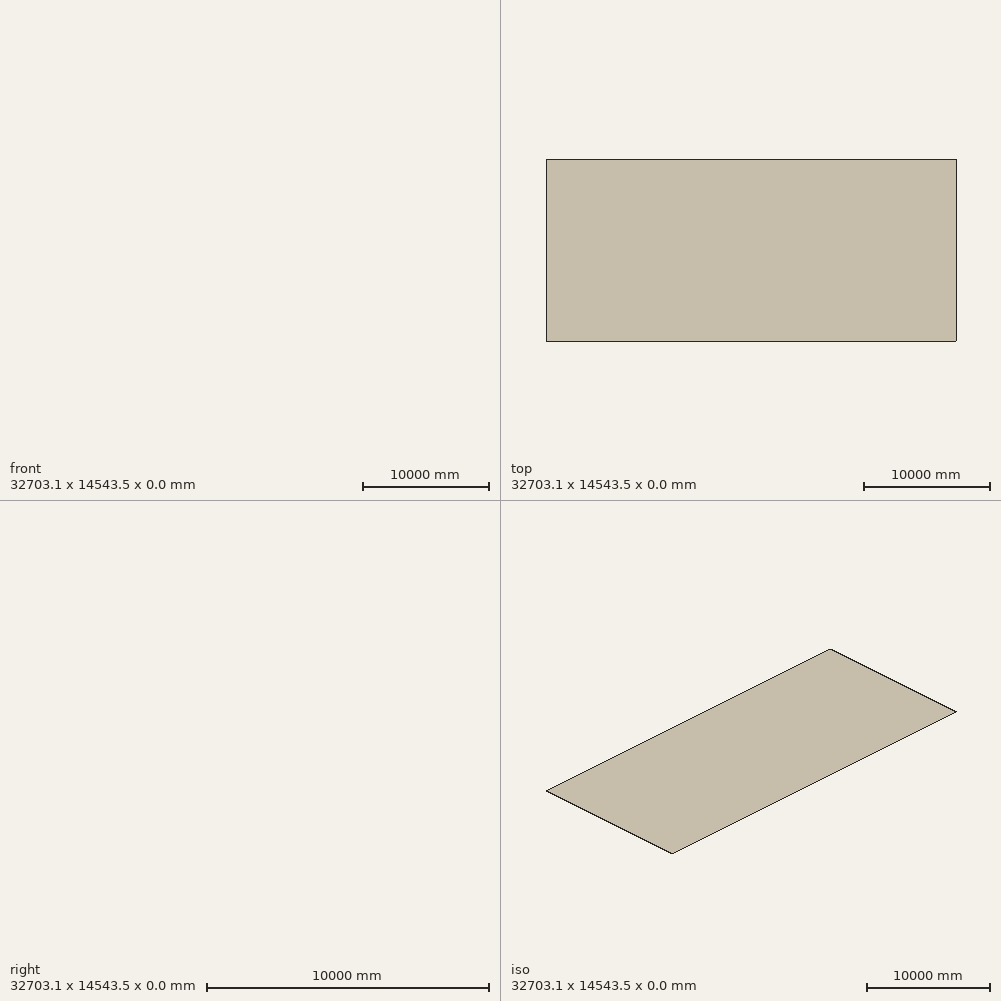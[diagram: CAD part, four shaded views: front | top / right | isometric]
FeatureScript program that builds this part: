
annotation { "Feature Type Name" : "Feature", "Feature Type Description" : "" }
export const myFeature = defineFeature(function(context is Context, id is Id, definition is map)
    precondition{}
    {
        {
            var Q0;
            Q0=qCreatedBy(makeId("Top.planeOp"),FACE);
            var sketch = newSketch(context, id + "F0", { "sketchPlane" : qUnion([Q0])});
            skLineSegment(sketch, "E0.bottom", {"start": v(0, 0) * mm, "end": v(32703.1, 0) * mm});
            skLineSegment(sketch, "E0.top", {"start": v(0, -14543.47) * mm, "end": v(32703.1, -14543.47) * mm});
            skLineSegment(sketch, "E0.left", {"start": v(0, 0) * mm, "end": v(0, -14543.47) * mm});
            skLineSegment(sketch, "E0.right", {"start": v(32703.1, 0) * mm, "end": v(32703.1, -14543.47) * mm});
            skSolve(sketch);
        }
        {
            var Q0;
            Q0=makeQuery(id+"F0.imprint","IMPRINT",FACE,{"disambiguationData":[TD([[makeQuery(id+"F0.imprint","IMPRINT",EDGE,{"derivedFrom":sQuery(id+"F0.wireOp",EDGE,"E0.bottom")}),-1.0]])]});
            extrude(context, id + "F1", {"entities" : qUnion([Q0]), "depth" : 0.03 * mm});
        }
    });
